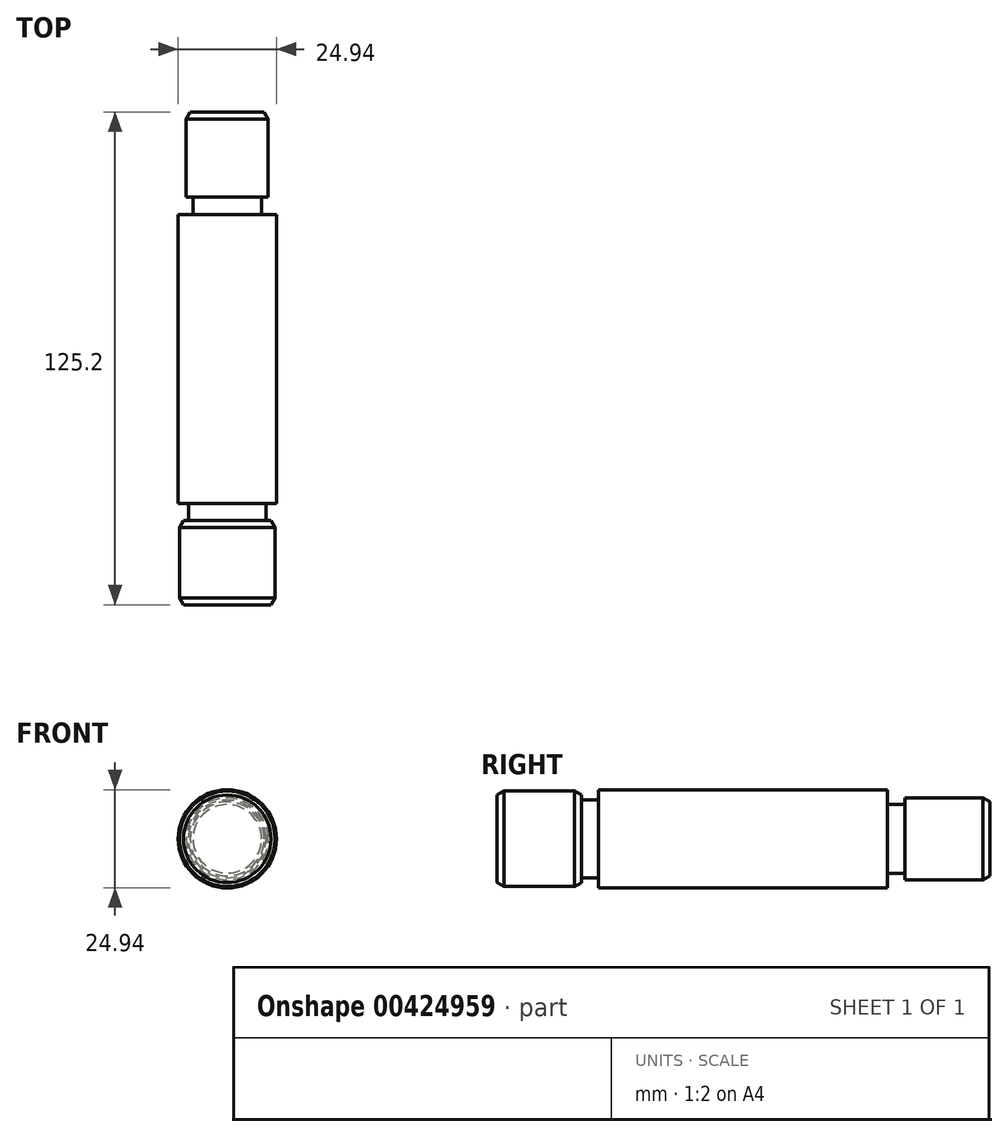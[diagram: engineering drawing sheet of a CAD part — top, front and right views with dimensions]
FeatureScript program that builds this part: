
annotation { "Feature Type Name" : "Feature", "Feature Type Description" : "" }
export const myFeature = defineFeature(function(context is Context, id is Id, definition is map)
    precondition{}
    {
        {
            var Q0;
            Q0=qCreatedBy(makeId("Front.planeOp"),FACE);
            var sketch = newSketch(context, id + "F0", { "sketchPlane" : qUnion([Q0])});
            skCircle(sketch, "E0", {"center": v(0, 0) * mm, "radius": 12.13 * mm});
            skSolve(sketch);
        }
        {
            var Q0;
            Q0 = qSketchRegion(id + "F0", true);
            extrude(context, id + "F1", {"entities" : qUnion([Q0]), "depth" : 21.44 * mm});
        }
        {
            var Q0;
            Q0=makeQuery(id+"F1.opExtrude","CAP_EDGE",EDGE,{"disambiguationData":[OSD([sQuery(id+"F0.wireOp",EDGE,"E0")])],"isStart":false});
            var Q1;
            Q1=makeQuery(id+"F1.opExtrude","CAP_EDGE",EDGE,{"disambiguationData":[OSD([sQuery(id+"F0.wireOp",EDGE,"E0")])],"isStart":true});
            chamfer(context, id + "F2", {"entities" : qUnion([Q0, Q1]), "chamferType" : ChamferType.OFFSET_ANGLE, "width" : 1.02 * mm, "oppositeDirection" : false, "angle" : 60 * degree, "tangentPropagation" : true});
        }
        {
            var Q0;
            Q0=makeQuery(id+"F1.opExtrude","CAP_FACE",FACE,{"disambiguationData":[OSD([sQuery(id+"F0.wireOp",EDGE,"E0")])],"isStart":true});
            var sketch = newSketch(context, id + "F3", { "sketchPlane" : qUnion([Q0])});
            skCircle(sketch, "E1", {"center": v(0, 0) * mm, "radius": 9.87 * mm});
            skSolve(sketch);
        }
        {
            var Q0;
            Q0 = qSketchRegion(id + "F3", true);
            extrude(context, id + "F4", {"entities" : qUnion([Q0]), "operationType" : NewBodyOperationType.ADD, "depth" : 4.32 * mm});
        }
        {
            var Q0;
            Q0=makeQuery(id+"F4.opExtrude","CAP_FACE",FACE,{"disambiguationData":[OSD([sQuery(id+"F3.wireOp",EDGE,"E1")])],"isStart":false});
            var sketch = newSketch(context, id + "F5", { "sketchPlane" : qUnion([Q0])});
            skCircle(sketch, "E2", {"center": v(0, 0) * mm, "radius": 12.47 * mm});
            skSolve(sketch);
        }
        {
            var Q0;
            Q0 = qSketchRegion(id + "F5", true);
            extrude(context, id + "F6", {"entities" : qUnion([Q0]), "operationType" : NewBodyOperationType.ADD, "depth" : 73.43 * mm});
        }
        {
            var Q0;
            Q0=makeQuery(id+"F6.opExtrude","CAP_FACE",FACE,{"disambiguationData":[OSD([sQuery(id+"F5.wireOp",EDGE,"E2")])],"isStart":false});
            var sketch = newSketch(context, id + "F7", { "sketchPlane" : qUnion([Q0])});
            skCircle(sketch, "E3", {"center": v(0, 0) * mm, "radius": 8.71 * mm});
            skSolve(sketch);
        }
        {
            var Q0;
            Q0 = qSketchRegion(id + "F7", true);
            extrude(context, id + "F8", {"entities" : qUnion([Q0]), "operationType" : NewBodyOperationType.ADD, "depth" : 4.42 * mm});
        }
        {
            var Q0;
            Q0=makeQuery(id+"F8.opExtrude","CAP_FACE",FACE,{"disambiguationData":[OSD([sQuery(id+"F7.wireOp",EDGE,"E3")])],"isStart":false});
            var sketch = newSketch(context, id + "F9", { "sketchPlane" : qUnion([Q0])});
            skCircle(sketch, "E4", {"center": v(0, 0) * mm, "radius": 10.41 * mm});
            skSolve(sketch);
        }
        {
            var Q0;
            Q0 = qSketchRegion(id + "F9", true);
            extrude(context, id + "F10", {"entities" : qUnion([Q0]), "operationType" : NewBodyOperationType.ADD, "depth" : 21.59 * mm});
        }
        {
            var Q0;
            Q0=makeQuery(id+"F10.opExtrude","CAP_EDGE",EDGE,{"disambiguationData":[OSD([sQuery(id+"F9.wireOp",EDGE,"E4")])],"isStart":false});
            chamfer(context, id + "F11", {"entities" : qUnion([Q0]), "chamferType" : ChamferType.OFFSET_ANGLE, "width" : 1.02 * mm, "oppositeDirection" : false, "angle" : 60 * degree, "tangentPropagation" : true});
        }
    });
